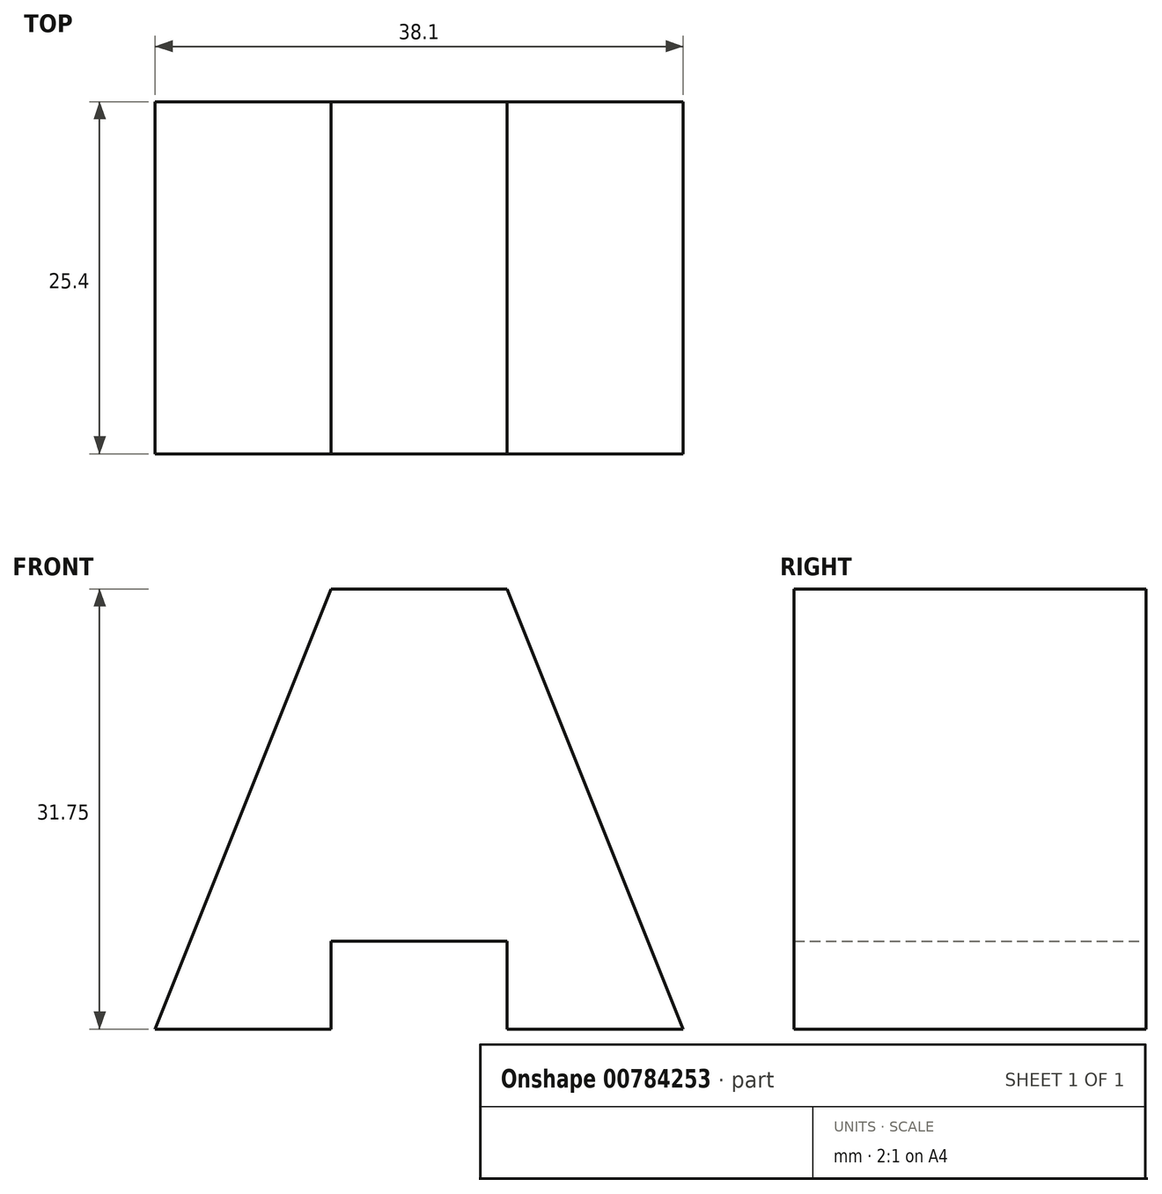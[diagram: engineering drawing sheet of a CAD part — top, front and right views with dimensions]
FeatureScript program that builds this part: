
annotation { "Feature Type Name" : "Feature", "Feature Type Description" : "" }
export const myFeature = defineFeature(function(context is Context, id is Id, definition is map)
    precondition{}
    {
        {
            var Q0;
            Q0=qCreatedBy(makeId("Front.planeOp"),FACE);
            var sketch = newSketch(context, id + "F0", { "sketchPlane" : qUnion([Q0])});
            skLineSegment(sketch, "E0", {"start": v(0, 0) * mm, "end": v(38.1, 0) * mm});
            skLineSegment(sketch, "E1", {"start": v(38.1, 0) * mm, "end": v(38.1, 31.75) * mm});
            skLineSegment(sketch, "E2", {"start": v(38.1, 31.75) * mm, "end": v(0, 31.75) * mm});
            skLineSegment(sketch, "E3", {"start": v(0, 31.75) * mm, "end": v(0, 0) * mm});
            skSolve(sketch);
        }
        {
            var Q0;
            Q0=makeQuery(id+"F0.imprint","IMPRINT",FACE,{"disambiguationData":[TD([[makeQuery(id+"F0.imprint","IMPRINT",EDGE,{"derivedFrom":sQuery(id+"F0.wireOp",EDGE,"E0")}),1.0]])]});
            extrude(context, id + "F1", {"entities" : qUnion([Q0]), "depth" : 25.4 * mm, "offsetDistance" : 25.4 * mm});
        }
        {
            var Q0;
            Q0=qCreatedBy(makeId("Front.planeOp"),FACE);
            var sketch = newSketch(context, id + "F2", { "sketchPlane" : qUnion([Q0])});
            skLineSegment(sketch, "E4", {"start": v(0, 0) * mm, "end": v(12.7, 0) * mm});
            skLineSegment(sketch, "E5", {"start": v(12.7, 0) * mm, "end": v(12.7, 6.35) * mm});
            skLineSegment(sketch, "E6", {"start": v(12.7, 6.35) * mm, "end": v(25.4, 6.35) * mm});
            skLineSegment(sketch, "E7", {"start": v(25.4, 6.35) * mm, "end": v(25.4, 0) * mm});
            skLineSegment(sketch, "E8", {"start": v(25.4, 0) * mm, "end": v(38.1, 0) * mm});
            skLineSegment(sketch, "E9", {"start": v(0, 0) * mm, "end": v(38.1, 0) * mm});
            skSolve(sketch);
        }
        {
            var Q0;
            Q0 = qSketchRegion(id + "F2", true);
            extrude(context, id + "F3", {"entities" : qUnion([Q0]), "operationType" : NewBodyOperationType.REMOVE, "depth" : 25.4 * mm, "offsetDistance" : 25.4 * mm});
        }
        {
            var Q0;
            Q0=makeQuery(id+"F1.opExtrude","CAP_FACE",FACE,{"disambiguationData":[OSD([sQuery(id+"F0.wireOp",EDGE,"E0"),sQuery(id+"F0.wireOp",EDGE,"E1"),sQuery(id+"F0.wireOp",EDGE,"E2"),sQuery(id+"F0.wireOp",EDGE,"E3")])],"isStart":false});
            var sketch = newSketch(context, id + "F4", { "sketchPlane" : qUnion([Q0])});
            skLineSegment(sketch, "E10", {"start": v(38.1, 0) * mm, "end": v(25.4, 0) * mm});
            skLineSegment(sketch, "E11", {"start": v(25.4, 0) * mm, "end": v(25.4, 31.75) * mm});
            skLineSegment(sketch, "E12", {"start": v(25.4, 31.75) * mm, "end": v(38.1, 0) * mm});
            skSolve(sketch);
        }
        {
            var Q0;
            {var subQ0=sQuery(id+"F4.wireOp",EDGE,"E12");Q0=makeQuery(id+"F4.imprint","IMPRINT",FACE,{"disambiguationData":[TD([[makeQuery(id+"F4.imprint","IMPRINT",EDGE,{"derivedFrom":subQ0}),1.0]])]});}
            extrude(context, id + "F5", {"entities" : qUnion([Q0]), "operationType" : NewBodyOperationType.REMOVE, "oppositeDirection" : true, "depth" : 25.4 * mm, "offsetDistance" : 25.4 * mm});
        }
        {
            var Q0;
            Q0=makeQuery(id+"F1.opExtrude","CAP_FACE",FACE,{"disambiguationData":[OSD([sQuery(id+"F0.wireOp",EDGE,"E0"),sQuery(id+"F0.wireOp",EDGE,"E1"),sQuery(id+"F0.wireOp",EDGE,"E2"),sQuery(id+"F0.wireOp",EDGE,"E3")])],"isStart":false});
            var sketch = newSketch(context, id + "F6", { "sketchPlane" : qUnion([Q0])});
            skLineSegment(sketch, "E13", {"start": v(0, 0) * mm, "end": v(12.7, 0) * mm});
            skLineSegment(sketch, "E14", {"start": v(12.7, 0) * mm, "end": v(12.7, 31.75) * mm});
            skLineSegment(sketch, "E15", {"start": v(12.7, 31.75) * mm, "end": v(0, 0) * mm});
            skSolve(sketch);
        }
        {
            var Q0;
            {var subQ0=sQuery(id+"F6.wireOp",EDGE,"E15");Q0=makeQuery(id+"F6.imprint","IMPRINT",FACE,{"disambiguationData":[TD([[makeQuery(id+"F6.imprint","IMPRINT",EDGE,{"derivedFrom":subQ0}),-1.0]])]});}
            extrude(context, id + "F7", {"entities" : qUnion([Q0]), "operationType" : NewBodyOperationType.REMOVE, "oppositeDirection" : true, "depth" : 25.4 * mm, "offsetDistance" : 25.4 * mm});
        }
    });
